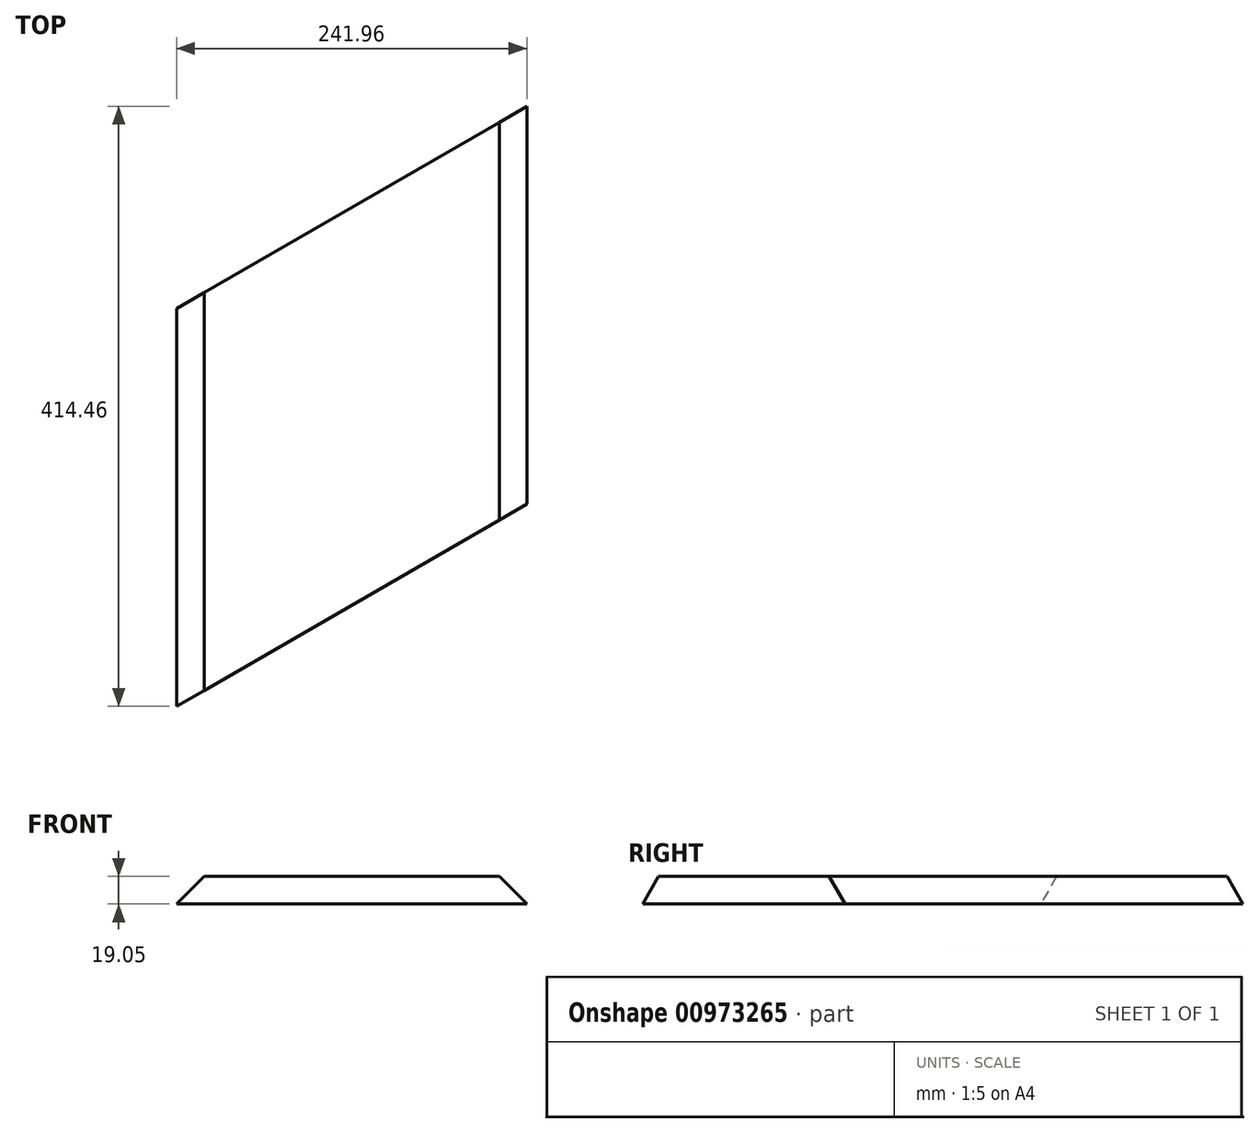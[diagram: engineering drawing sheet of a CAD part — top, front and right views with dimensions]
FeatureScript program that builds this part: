
annotation { "Feature Type Name" : "Feature", "Feature Type Description" : "" }
export const myFeature = defineFeature(function(context is Context, id is Id, definition is map)
    precondition{}
    {
        {
            var Q0;
            Q0=qCreatedBy(makeId("Top.planeOp"),FACE);
            var sketch = newSketch(context, id + "F0", { "sketchPlane" : qUnion([Q0])});
            skLineSegment(sketch, "E0.left", {"start": v(120.98, -67.53) * mm, "end": v(120.98, 207.23) * mm});
            skLineSegment(sketch, "E0.right", {"start": v(-120.98, -207.23) * mm, "end": v(-120.98, 67.53) * mm});
            skPoint(sketch, "E0.middle", {"position": v(0, 0) * mm});
            skLineSegment(sketch, "E1", {"start": v(-120.98, -207.23) * mm, "end": v(120.98, -67.53) * mm});
            skLineSegment(sketch, "E2", {"start": v(120.98, 207.23) * mm, "end": v(-120.98, 67.53) * mm});
            skPoint(sketch, "E3.orphan", {"position": v(-120.98, 248.36) * mm});
            skPoint(sketch, "E4.end.orphan", {"position": v(120.98, -248.36) * mm});
            skSolve(sketch);
        }
        {
            var Q0;
            Q0 = qSketchRegion(id + "F0", true);
            extrude(context, id + "F1", {"entities" : qUnion([Q0]), "depth" : 19.05 * mm, "offsetDistance" : 25.4 * mm});
        }
        {
            var Q0;
            Q0=makeQuery(id+"F1.opExtrude","CAP_EDGE",EDGE,{"disambiguationData":[OSD([sQuery(id+"F0.wireOp",EDGE,"E0.right")])],"isStart":false});
            chamfer(context, id + "F2", {"entities" : qUnion([Q0]), "width" : 19.05 * mm, "tangentPropagation" : true});
        }
        {
            var Q0;
            Q0=makeQuery(id+"F1.opExtrude","CAP_EDGE",EDGE,{"disambiguationData":[OSD([sQuery(id+"F0.wireOp",EDGE,"E0.left")])],"isStart":false});
            chamfer(context, id + "F3", {"entities" : qUnion([Q0]), "width" : 19.05 * mm, "tangentPropagation" : true});
        }
    });
